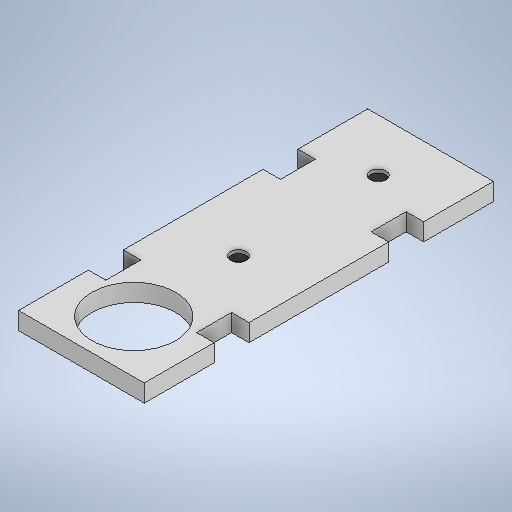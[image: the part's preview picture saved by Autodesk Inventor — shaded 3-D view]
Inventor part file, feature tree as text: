
AUTODESK INVENTOR PART (.ipt)
format: ipt  version: 2025.2 (Build 292293000, 293)  size: 275,456 bytes
history: native  units: mm
features: extrude x2, sketch x2
ambient origin geometry x8: Origin, YZ Plane, XZ Plane, XY Plane, X Axis, Y Axis, Z Axis, Center Point
bodies: Solid1 (feature_tree)
feature tree (4):
  extrude  "Extrusion1"  Depth=100.0mm
  extrude  "Extrusion2"  Depth=20.0mm
  sketch  "Sketch2"  dims[d0=36.0mm d1=100.0mm]
  sketch  "Sketch3"  dims[d2=20.0mm d3=20.0mm d4=10.0mm d5=5.0mm d6=10.0mm d7=5.0mm d8=5.0mm d9=15.0mm d10=24.0mm d15=5.0mm d16=0.0mm d17=30.0mm d18=10.1mm d19=40.0mm d20=10.1mm d21=4.5mm d22=4.5mm d23=1.0mm d24=0.0mm]
